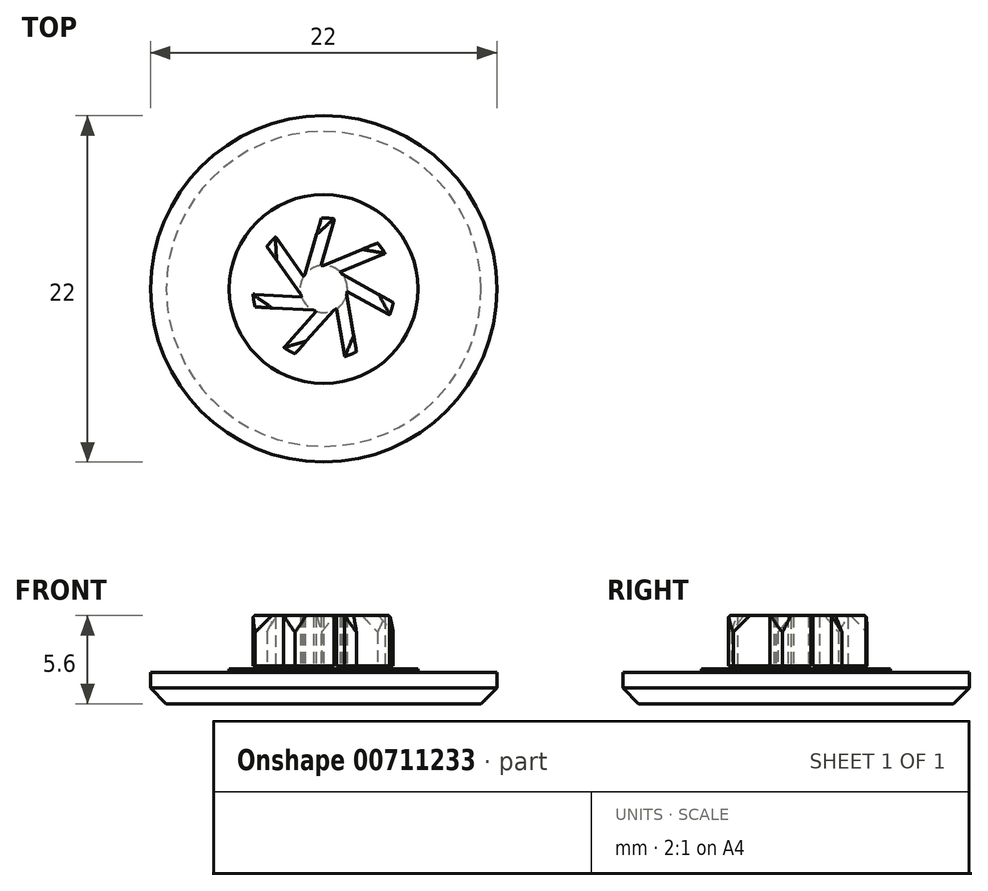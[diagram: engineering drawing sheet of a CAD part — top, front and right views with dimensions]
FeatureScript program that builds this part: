
annotation { "Feature Type Name" : "Feature", "Feature Type Description" : "" }
export const myFeature = defineFeature(function(context is Context, id is Id, definition is map)
    precondition{}
    {
        {
            var Q0;
            Q0=qCreatedBy(makeId("Top.planeOp"),FACE);
            var sketch = newSketch(context, id + "F0", { "sketchPlane" : qUnion([Q0])});
            skCircle(sketch, "E0", {"center": v(0, 0) * mm, "radius": 11 * mm});
            skSolve(sketch);
        }
        {
            var Q0;
            Q0=makeQuery(id+"F0.imprint","IMPRINT",FACE,{"disambiguationData":[TD([[makeQuery(id+"F0.imprint","IMPRINT",EDGE,{"derivedFrom":sQuery(id+"F0.wireOp",EDGE,"E0")}),1.0]])]});
            extrude(context, id + "F1", {"entities" : qUnion([Q0]), "depth" : 2 * mm, "offsetDistance" : 25 * mm});
        }
        {
            var Q0;
            Q0=makeQuery(id+"F1.opExtrude","CAP_EDGE",EDGE,{"disambiguationData":[OSD([sQuery(id+"F0.wireOp",EDGE,"E0")])],"isStart":true});
            chamfer(context, id + "F2", {"entities" : qUnion([Q0]), "width" : 1 * mm, "tangentPropagation" : true});
        }
        {
            var Q0;
            Q0=makeQuery(id+"F1.opExtrude","CAP_FACE",FACE,{"disambiguationData":[OSD([sQuery(id+"F0.wireOp",EDGE,"E0")])],"isStart":false});
            var sketch = newSketch(context, id + "F3", { "sketchPlane" : qUnion([Q0])});
            skCircle(sketch, "E1", {"center": v(0, 0) * mm, "radius": 6 * mm});
            skSolve(sketch);
        }
        {
            var Q0;
            Q0=makeQuery(id+"F3.imprint","IMPRINT",FACE,{"disambiguationData":[TD([[makeQuery(id+"F3.imprint","IMPRINT",EDGE,{"derivedFrom":sQuery(id+"F3.wireOp",EDGE,"E1")}),1.0]])]});
            extrude(context, id + "F4", {"entities" : qUnion([Q0]), "operationType" : NewBodyOperationType.ADD, "depth" : .2 * mm, "offsetDistance" : 25 * mm});
        }
        {
            var Q0;
            Q0=makeQuery(id+"F4.opExtrude","CAP_FACE",FACE,{"disambiguationData":[OSD([sQuery(id+"F3.wireOp",EDGE,"E1")])],"isStart":false});
            var sketch = newSketch(context, id + "F5", { "sketchPlane" : qUnion([Q0])});
            skCircle(sketch, "E2", {"center": v(0, 0) * mm, "radius": 4.5 * mm});
            skCircle(sketch, "E3", {"center": v(0, 0) * mm, "radius": 1.5 * mm});
            skCircle(sketch, "E4.0", {"center": v(0, 0) * mm, "radius": 11 * mm});
            skLineSegment(sketch, "E5", {"start": v(0, 1.5) * mm, "end": v(3.43, 2.92) * mm});
            skLineSegment(sketch, "E6.0", {"start": v(1.05, 1.07) * mm, "end": v(3.9, 2.25) * mm});
            skLineSegment(sketch, "E7.1.0", {"start": v(-1.17, 0.94) * mm, "end": v(-0.15, 4.5) * mm});
            skLineSegment(sketch, "E7.1.1", {"start": v(-0.18, 1.49) * mm, "end": v(0.67, 4.45) * mm});
            skLineSegment(sketch, "E7.2.0", {"start": v(-1.46, -0.33) * mm, "end": v(-3.6, 2.69) * mm});
            skLineSegment(sketch, "E7.2.1", {"start": v(-1.28, 0.79) * mm, "end": v(-3.06, 3.3) * mm});
            skLineSegment(sketch, "E7.3.0", {"start": v(-0.65, -1.35) * mm, "end": v(-4.35, -1.14) * mm});
            skLineSegment(sketch, "E7.3.1", {"start": v(-1.41, -0.5) * mm, "end": v(-4.49, -0.33) * mm});
            skLineSegment(sketch, "E7.4.0", {"start": v(0.65, -1.35) * mm, "end": v(-1.82, -4.12) * mm});
            skLineSegment(sketch, "E7.4.1", {"start": v(-0.48, -1.42) * mm, "end": v(-2.54, -3.72) * mm});
            skLineSegment(sketch, "E7.5.0", {"start": v(1.46, -0.33) * mm, "end": v(2.08, -3.99) * mm});
            skLineSegment(sketch, "E7.5.1", {"start": v(0.8, -1.26) * mm, "end": v(1.32, -4.3) * mm});
            skLineSegment(sketch, "E7.6.0", {"start": v(1.17, 0.94) * mm, "end": v(4.42, -0.86) * mm});
            skLineSegment(sketch, "E7.6.1", {"start": v(1.5, -0.16) * mm, "end": v(4.19, -1.65) * mm});
            skSolve(sketch);
        }
        {
            var Q0;
            {var subQ0=sQuery(id+"F5.wireOp",EDGE,"E5");Q0=makeQuery(id+"F5.imprint","IMPRINT",FACE,{"disambiguationData":[TD([[makeQuery(id+"F5.imprint","IMPRINT",EDGE,{"derivedFrom":subQ0}),-1.0]])]});}
            var Q1;
            {var subQ0=sQuery(id+"F5.wireOp",EDGE,"E7.1.0");Q1=makeQuery(id+"F5.imprint","IMPRINT",FACE,{"disambiguationData":[TD([[makeQuery(id+"F5.imprint","IMPRINT",EDGE,{"derivedFrom":subQ0}),-1.0]])]});}
            var Q2;
            {var subQ0=sQuery(id+"F5.wireOp",EDGE,"E7.2.0");Q2=makeQuery(id+"F5.imprint","IMPRINT",FACE,{"disambiguationData":[TD([[makeQuery(id+"F5.imprint","IMPRINT",EDGE,{"derivedFrom":subQ0}),-1.0]])]});}
            var Q3;
            {var subQ0=sQuery(id+"F5.wireOp",EDGE,"E7.3.0");Q3=makeQuery(id+"F5.imprint","IMPRINT",FACE,{"disambiguationData":[TD([[makeQuery(id+"F5.imprint","IMPRINT",EDGE,{"derivedFrom":subQ0}),-1.0]])]});}
            var Q4;
            {var subQ0=sQuery(id+"F5.wireOp",EDGE,"E7.4.0");Q4=makeQuery(id+"F5.imprint","IMPRINT",FACE,{"disambiguationData":[TD([[makeQuery(id+"F5.imprint","IMPRINT",EDGE,{"derivedFrom":subQ0}),-1.0]])]});}
            var Q5;
            {var subQ0=sQuery(id+"F5.wireOp",EDGE,"E7.5.0");Q5=makeQuery(id+"F5.imprint","IMPRINT",FACE,{"disambiguationData":[TD([[makeQuery(id+"F5.imprint","IMPRINT",EDGE,{"derivedFrom":subQ0}),-1.0]])]});}
            var Q6;
            {var subQ0=sQuery(id+"F5.wireOp",EDGE,"E7.6.0");Q6=makeQuery(id+"F5.imprint","IMPRINT",FACE,{"disambiguationData":[TD([[makeQuery(id+"F5.imprint","IMPRINT",EDGE,{"derivedFrom":subQ0}),-1.0]])]});}
            var Q7;
            {var subQ0=sQuery(id+"F5.wireOp",EDGE,"E3");var subQ8=makeQuery(id+"F5.imprint","INTERSECT",VERTEX,{"derivedFrom":[subQ0,sQuery(id+"F5.wireOp",EDGE,"E6.0")]});Q7=makeQuery(id+"F5.imprint","IMPRINT",FACE,{"disambiguationData":[TD([[makeQuery(id+"F5.imprint","IMPRINT",EDGE,{"disambiguationData":[TD([[subQ8,1.0]])],"derivedFrom":subQ0}),1.0]])]});}
            extrude(context, id + "F6", {"entities" : qUnion([Q0, Q1, Q2, Q3, Q4, Q5, Q6, Q7]), "operationType" : NewBodyOperationType.ADD, "depth" : 3.4 * mm, "offsetDistance" : 25 * mm});
        }
        {
            var Q0;
            {var subQ0=sQuery(id+"F5.wireOp",EDGE,"E7.2.0");Q0=makeQuery(id+"F5.imprint","IMPRINT",FACE,{"disambiguationData":[TD([[makeQuery(id+"F5.imprint","IMPRINT",EDGE,{"derivedFrom":subQ0}),-1.0]])]});}
            var Q1;
            {var subQ0=sQuery(id+"F5.wireOp",EDGE,"E7.3.0");Q1=makeQuery(id+"F5.imprint","IMPRINT",FACE,{"disambiguationData":[TD([[makeQuery(id+"F5.imprint","IMPRINT",EDGE,{"derivedFrom":subQ0}),-1.0]])]});}
            var Q2;
            {var subQ0=sQuery(id+"F5.wireOp",EDGE,"E7.4.0");Q2=makeQuery(id+"F5.imprint","IMPRINT",FACE,{"disambiguationData":[TD([[makeQuery(id+"F5.imprint","IMPRINT",EDGE,{"derivedFrom":subQ0}),-1.0]])]});}
            var Q3;
            {var subQ0=sQuery(id+"F5.wireOp",EDGE,"E7.5.0");Q3=makeQuery(id+"F5.imprint","IMPRINT",FACE,{"disambiguationData":[TD([[makeQuery(id+"F5.imprint","IMPRINT",EDGE,{"derivedFrom":subQ0}),-1.0]])]});}
            var Q4;
            {var subQ0=sQuery(id+"F5.wireOp",EDGE,"E7.6.0");Q4=makeQuery(id+"F5.imprint","IMPRINT",FACE,{"disambiguationData":[TD([[makeQuery(id+"F5.imprint","IMPRINT",EDGE,{"derivedFrom":subQ0}),-1.0]])]});}
            var Q5;
            {var subQ0=sQuery(id+"F5.wireOp",EDGE,"E5");Q5=makeQuery(id+"F5.imprint","IMPRINT",FACE,{"disambiguationData":[TD([[makeQuery(id+"F5.imprint","IMPRINT",EDGE,{"derivedFrom":subQ0}),-1.0]])]});}
            var Q6;
            {var subQ0=sQuery(id+"F5.wireOp",EDGE,"E7.1.0");Q6=makeQuery(id+"F5.imprint","IMPRINT",FACE,{"disambiguationData":[TD([[makeQuery(id+"F5.imprint","IMPRINT",EDGE,{"derivedFrom":subQ0}),-1.0]])]});}
            extrude(context, id + "F7", {"entities" : qUnion([Q0, Q1, Q2, Q3, Q4, Q5, Q6]), "operationType" : NewBodyOperationType.REMOVE, "depth" : .2 * mm, "offsetDistance" : 25 * mm});
        }
        {
            var Q0;
            {var subQ0=sQuery(id+"F5.wireOp",EDGE,"E2");Q0=makeQuery(id+"F6.opExtrude","CAP_EDGE",EDGE,{"disambiguationData":[OSD([subQ0]),TDD([makeQuery(id+"F5.imprint","IMPRINT",EDGE,{"disambiguationData":[TD([[makeQuery(id+"F5.imprint","INTERSECT",VERTEX,{"derivedFrom":[subQ0,sQuery(id+"F5.wireOp",EDGE,"E7.4.0")]}),1.0]])],"derivedFrom":subQ0})])],"isStart":false});}
            var Q1;
            {var subQ0=sQuery(id+"F5.wireOp",EDGE,"E2");Q1=makeQuery(id+"F6.opExtrude","CAP_EDGE",EDGE,{"disambiguationData":[OSD([subQ0]),TDD([makeQuery(id+"F5.imprint","IMPRINT",EDGE,{"disambiguationData":[TD([[makeQuery(id+"F5.imprint","INTERSECT",VERTEX,{"derivedFrom":[subQ0,sQuery(id+"F5.wireOp",EDGE,"E7.5.0")]}),1.0]])],"derivedFrom":subQ0})])],"isStart":false});}
            var Q2;
            {var subQ0=sQuery(id+"F5.wireOp",EDGE,"E2");Q2=makeQuery(id+"F6.opExtrude","CAP_EDGE",EDGE,{"disambiguationData":[OSD([subQ0]),TDD([makeQuery(id+"F5.imprint","IMPRINT",EDGE,{"disambiguationData":[TD([[makeQuery(id+"F5.imprint","INTERSECT",VERTEX,{"derivedFrom":[subQ0,sQuery(id+"F5.wireOp",EDGE,"E7.6.0")]}),1.0]])],"derivedFrom":subQ0})])],"isStart":false});}
            var Q3;
            {var subQ0=sQuery(id+"F5.wireOp",EDGE,"E2");Q3=makeQuery(id+"F6.opExtrude","CAP_EDGE",EDGE,{"disambiguationData":[OSD([subQ0]),TDD([makeQuery(id+"F5.imprint","IMPRINT",EDGE,{"disambiguationData":[TD([[makeQuery(id+"F5.imprint","INTERSECT",VERTEX,{"derivedFrom":[subQ0,sQuery(id+"F5.wireOp",EDGE,"E5")]}),1.0]])],"derivedFrom":subQ0})])],"isStart":false});}
            var Q4;
            {var subQ0=sQuery(id+"F5.wireOp",EDGE,"E2");Q4=makeQuery(id+"F6.opExtrude","CAP_EDGE",EDGE,{"disambiguationData":[OSD([subQ0]),TDD([makeQuery(id+"F5.imprint","IMPRINT",EDGE,{"disambiguationData":[TD([[makeQuery(id+"F5.imprint","INTERSECT",VERTEX,{"derivedFrom":[subQ0,sQuery(id+"F5.wireOp",EDGE,"E7.1.0")]}),1.0]])],"derivedFrom":subQ0})])],"isStart":false});}
            var Q5;
            {var subQ0=sQuery(id+"F5.wireOp",EDGE,"E2");Q5=makeQuery(id+"F6.opExtrude","CAP_EDGE",EDGE,{"disambiguationData":[OSD([subQ0]),TDD([makeQuery(id+"F5.imprint","IMPRINT",EDGE,{"disambiguationData":[TD([[makeQuery(id+"F5.imprint","INTERSECT",VERTEX,{"derivedFrom":[subQ0,sQuery(id+"F5.wireOp",EDGE,"E7.2.0")]}),1.0]])],"derivedFrom":subQ0})])],"isStart":false});}
            var Q6;
            {var subQ0=sQuery(id+"F5.wireOp",EDGE,"E2");Q6=makeQuery(id+"F6.opExtrude","CAP_EDGE",EDGE,{"disambiguationData":[OSD([subQ0]),TDD([makeQuery(id+"F5.imprint","IMPRINT",EDGE,{"disambiguationData":[TD([[makeQuery(id+"F5.imprint","INTERSECT",VERTEX,{"derivedFrom":[subQ0,sQuery(id+"F5.wireOp",EDGE,"E7.3.0")]}),1.0]])],"derivedFrom":subQ0})])],"isStart":false});}
            chamfer(context, id + "F8", {"entities" : qUnion([Q0, Q1, Q2, Q3, Q4, Q5, Q6]), "width" : .1 * mm, "tangentPropagation" : true});
        }
        {
            var Q0;
            {var subQ0=sQuery(id+"F5.wireOp",EDGE,"E7.3.0");var subQ1=sQuery(id+"F5.wireOp",EDGE,"E2");Q0=makeQuery(id+"F8.opChamfer","BLEND_EDGE",EDGE,{"blendedFrom":[makeQuery(id+"F6.opExtrude","CAP_EDGE",EDGE,{"disambiguationData":[OSD([subQ1]),TDD([makeQuery(id+"F5.imprint","IMPRINT",EDGE,{"disambiguationData":[TD([[makeQuery(id+"F5.imprint","INTERSECT",VERTEX,{"derivedFrom":[subQ1,subQ0]}),1.0]])],"derivedFrom":subQ1})])],"isStart":false}),makeQuery(id+"F6.opExtrude","SWEPT_FACE",FACE,{"disambiguationData":[OSD([subQ0])]})],"blendedInto":[makeQuery(id+"F6.opExtrude","SWEPT_FACE",FACE,{"disambiguationData":[OSD([subQ0])]})]});}
            var Q1;
            {var subQ0=sQuery(id+"F5.wireOp",EDGE,"E7.4.0");var subQ1=sQuery(id+"F5.wireOp",EDGE,"E2");Q1=makeQuery(id+"F8.opChamfer","BLEND_EDGE",EDGE,{"blendedFrom":[makeQuery(id+"F6.opExtrude","CAP_EDGE",EDGE,{"disambiguationData":[OSD([subQ1]),TDD([makeQuery(id+"F5.imprint","IMPRINT",EDGE,{"disambiguationData":[TD([[makeQuery(id+"F5.imprint","INTERSECT",VERTEX,{"derivedFrom":[subQ1,subQ0]}),1.0]])],"derivedFrom":subQ1})])],"isStart":false}),makeQuery(id+"F6.opExtrude","SWEPT_FACE",FACE,{"disambiguationData":[OSD([subQ0])]})],"blendedInto":[makeQuery(id+"F6.opExtrude","SWEPT_FACE",FACE,{"disambiguationData":[OSD([subQ0])]})]});}
            var Q2;
            {var subQ0=sQuery(id+"F5.wireOp",EDGE,"E7.5.0");var subQ1=sQuery(id+"F5.wireOp",EDGE,"E2");Q2=makeQuery(id+"F8.opChamfer","BLEND_EDGE",EDGE,{"blendedFrom":[makeQuery(id+"F6.opExtrude","CAP_EDGE",EDGE,{"disambiguationData":[OSD([subQ1]),TDD([makeQuery(id+"F5.imprint","IMPRINT",EDGE,{"disambiguationData":[TD([[makeQuery(id+"F5.imprint","INTERSECT",VERTEX,{"derivedFrom":[subQ1,subQ0]}),1.0]])],"derivedFrom":subQ1})])],"isStart":false}),makeQuery(id+"F6.opExtrude","SWEPT_FACE",FACE,{"disambiguationData":[OSD([subQ0])]})],"blendedInto":[makeQuery(id+"F6.opExtrude","SWEPT_FACE",FACE,{"disambiguationData":[OSD([subQ0])]})]});}
            var Q3;
            {var subQ0=sQuery(id+"F5.wireOp",EDGE,"E7.6.0");var subQ1=sQuery(id+"F5.wireOp",EDGE,"E2");Q3=makeQuery(id+"F8.opChamfer","BLEND_EDGE",EDGE,{"blendedFrom":[makeQuery(id+"F6.opExtrude","CAP_EDGE",EDGE,{"disambiguationData":[OSD([subQ1]),TDD([makeQuery(id+"F5.imprint","IMPRINT",EDGE,{"disambiguationData":[TD([[makeQuery(id+"F5.imprint","INTERSECT",VERTEX,{"derivedFrom":[subQ1,subQ0]}),1.0]])],"derivedFrom":subQ1})])],"isStart":false}),makeQuery(id+"F6.opExtrude","SWEPT_FACE",FACE,{"disambiguationData":[OSD([subQ0])]})],"blendedInto":[makeQuery(id+"F6.opExtrude","SWEPT_FACE",FACE,{"disambiguationData":[OSD([subQ0])]})]});}
            var Q4;
            {var subQ0=sQuery(id+"F5.wireOp",EDGE,"E5");var subQ1=sQuery(id+"F5.wireOp",EDGE,"E2");Q4=makeQuery(id+"F8.opChamfer","BLEND_EDGE",EDGE,{"blendedFrom":[makeQuery(id+"F6.opExtrude","CAP_EDGE",EDGE,{"disambiguationData":[OSD([subQ1]),TDD([makeQuery(id+"F5.imprint","IMPRINT",EDGE,{"disambiguationData":[TD([[makeQuery(id+"F5.imprint","INTERSECT",VERTEX,{"derivedFrom":[subQ1,subQ0]}),1.0]])],"derivedFrom":subQ1})])],"isStart":false}),makeQuery(id+"F6.opExtrude","SWEPT_FACE",FACE,{"disambiguationData":[OSD([subQ0])]})],"blendedInto":[makeQuery(id+"F6.opExtrude","SWEPT_FACE",FACE,{"disambiguationData":[OSD([subQ0])]})]});}
            var Q5;
            {var subQ0=sQuery(id+"F5.wireOp",EDGE,"E7.1.0");var subQ1=sQuery(id+"F5.wireOp",EDGE,"E2");Q5=makeQuery(id+"F8.opChamfer","BLEND_EDGE",EDGE,{"blendedFrom":[makeQuery(id+"F6.opExtrude","CAP_EDGE",EDGE,{"disambiguationData":[OSD([subQ1]),TDD([makeQuery(id+"F5.imprint","IMPRINT",EDGE,{"disambiguationData":[TD([[makeQuery(id+"F5.imprint","INTERSECT",VERTEX,{"derivedFrom":[subQ1,subQ0]}),1.0]])],"derivedFrom":subQ1})])],"isStart":false}),makeQuery(id+"F6.opExtrude","SWEPT_FACE",FACE,{"disambiguationData":[OSD([subQ0])]})],"blendedInto":[makeQuery(id+"F6.opExtrude","SWEPT_FACE",FACE,{"disambiguationData":[OSD([subQ0])]})]});}
            var Q6;
            {var subQ0=sQuery(id+"F5.wireOp",EDGE,"E7.2.0");var subQ1=sQuery(id+"F5.wireOp",EDGE,"E2");Q6=makeQuery(id+"F8.opChamfer","BLEND_EDGE",EDGE,{"blendedFrom":[makeQuery(id+"F6.opExtrude","CAP_EDGE",EDGE,{"disambiguationData":[OSD([subQ1]),TDD([makeQuery(id+"F5.imprint","IMPRINT",EDGE,{"disambiguationData":[TD([[makeQuery(id+"F5.imprint","INTERSECT",VERTEX,{"derivedFrom":[subQ1,subQ0]}),1.0]])],"derivedFrom":subQ1})])],"isStart":false}),makeQuery(id+"F6.opExtrude","SWEPT_FACE",FACE,{"disambiguationData":[OSD([subQ0])]})],"blendedInto":[makeQuery(id+"F6.opExtrude","SWEPT_FACE",FACE,{"disambiguationData":[OSD([subQ0])]})]});}
            chamfer(context, id + "F9", {"entities" : qUnion([Q0, Q1, Q2, Q3, Q4, Q5, Q6]), "width" : .8 * mm, "tangentPropagation" : true});
        }
    });
